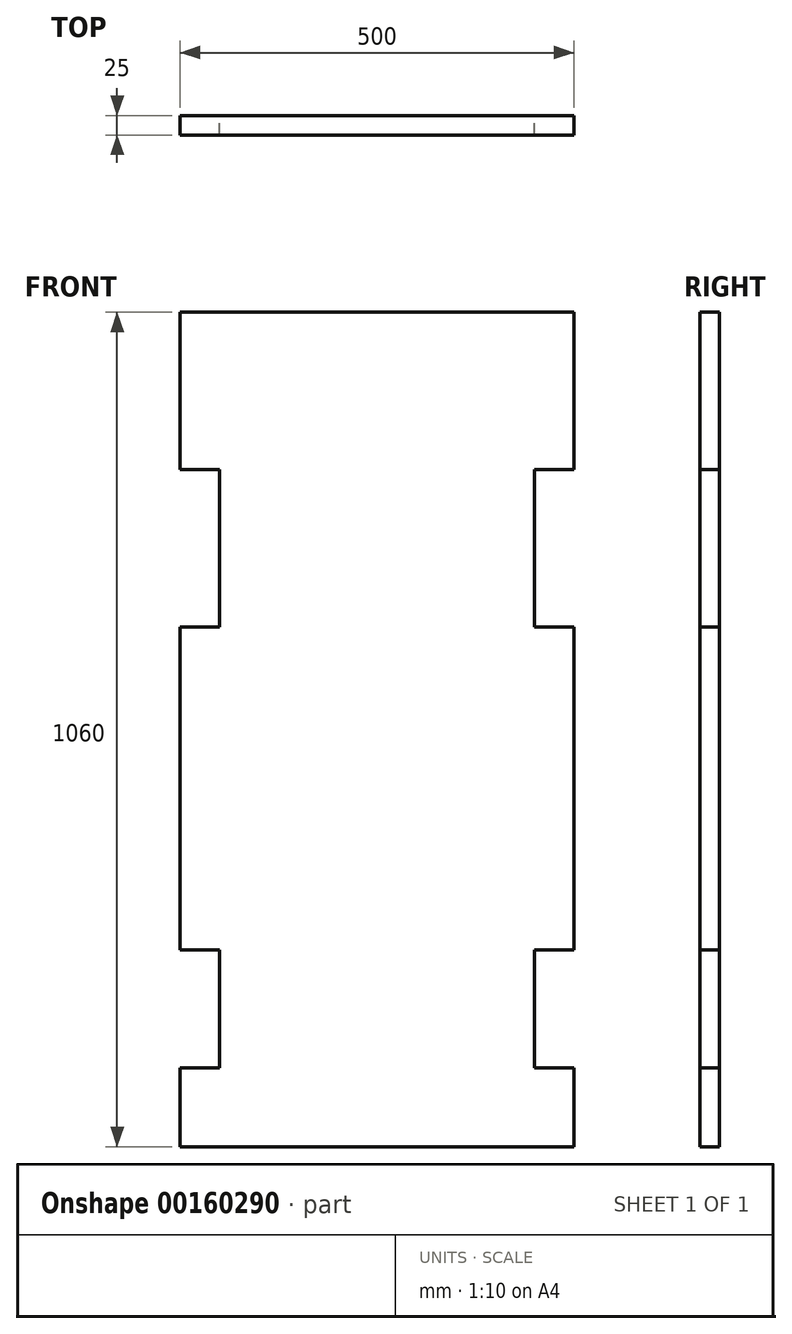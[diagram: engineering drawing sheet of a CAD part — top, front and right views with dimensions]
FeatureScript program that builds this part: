
annotation { "Feature Type Name" : "Feature", "Feature Type Description" : "" }
export const myFeature = defineFeature(function(context is Context, id is Id, definition is map)
    precondition{}
    {
        {
            var Q0;
            Q0=qCreatedBy(makeId("Front.planeOp"),FACE);
            var sketch = newSketch(context, id + "F0", { "sketchPlane" : qUnion([Q0])});
            skLineSegment(sketch, "E0", {"start": v(-50, 810) * mm, "end": v(-50, 610) * mm});
            skLineSegment(sketch, "E1", {"start": v(-50, -150) * mm, "end": v(-50, -250) * mm});
            skLineSegment(sketch, "E2", {"start": v(-50, 810) * mm, "end": v(450, 810) * mm});
            skLineSegment(sketch, "E3", {"start": v(-50, 610) * mm, "end": v(0, 610) * mm});
            skLineSegment(sketch, "E4", {"start": v(-50, 410) * mm, "end": v(0, 410) * mm});
            skLineSegment(sketch, "E5", {"start": v(-50, 0) * mm, "end": v(0, 0) * mm});
            skLineSegment(sketch, "E6", {"start": v(-50, -150) * mm, "end": v(0, -150) * mm});
            skLineSegment(sketch, "E7", {"start": v(0, 610) * mm, "end": v(0, 410) * mm});
            skLineSegment(sketch, "E8", {"start": v(0, 0) * mm, "end": v(0, -150) * mm});
            skLineSegment(sketch, "E9", {"start": v(-50, -250) * mm, "end": v(450, -250) * mm});
            skLineSegment(sketch, "E10", {"start": v(450, 810) * mm, "end": v(450, 610) * mm});
            skLineSegment(sketch, "E11", {"start": v(450, 610) * mm, "end": v(400, 610) * mm});
            skLineSegment(sketch, "E12", {"start": v(400, 610) * mm, "end": v(400, 410) * mm});
            skLineSegment(sketch, "E13", {"start": v(400, 410) * mm, "end": v(450, 410) * mm});
            skLineSegment(sketch, "E14", {"start": v(450, 0) * mm, "end": v(400, 0) * mm});
            skLineSegment(sketch, "E15", {"start": v(400, 0) * mm, "end": v(400, -150) * mm});
            skLineSegment(sketch, "E16", {"start": v(400, -150) * mm, "end": v(450, -150) * mm});
            skLineSegment(sketch, "E17", {"start": v(450, -150) * mm, "end": v(450, -250) * mm});
            skLineSegment(sketch, "E18", {"start": v(-50, 410) * mm, "end": v(-50, 200) * mm});
            skLineSegment(sketch, "E19", {"start": v(-50, 200) * mm, "end": v(-50, 0) * mm});
            skLineSegment(sketch, "E20", {"start": v(450, 410) * mm, "end": v(450, 200) * mm});
            skLineSegment(sketch, "E21", {"start": v(450, 200) * mm, "end": v(450, 0) * mm});
            skLineSegment(sketch, "E22", {"start": v(-50, 200) * mm, "end": v(-20, 200) * mm});
            skLineSegment(sketch, "E23", {"start": v(450, 200) * mm, "end": v(420, 200) * mm});
            skSolve(sketch);
        }
        {
            var Q0;
            Q0 = qSketchRegion(id + "F0", true);
            extrude(context, id + "F1", {"entities" : qUnion([Q0]), "depth" : 25 * mm});
        }
    });
